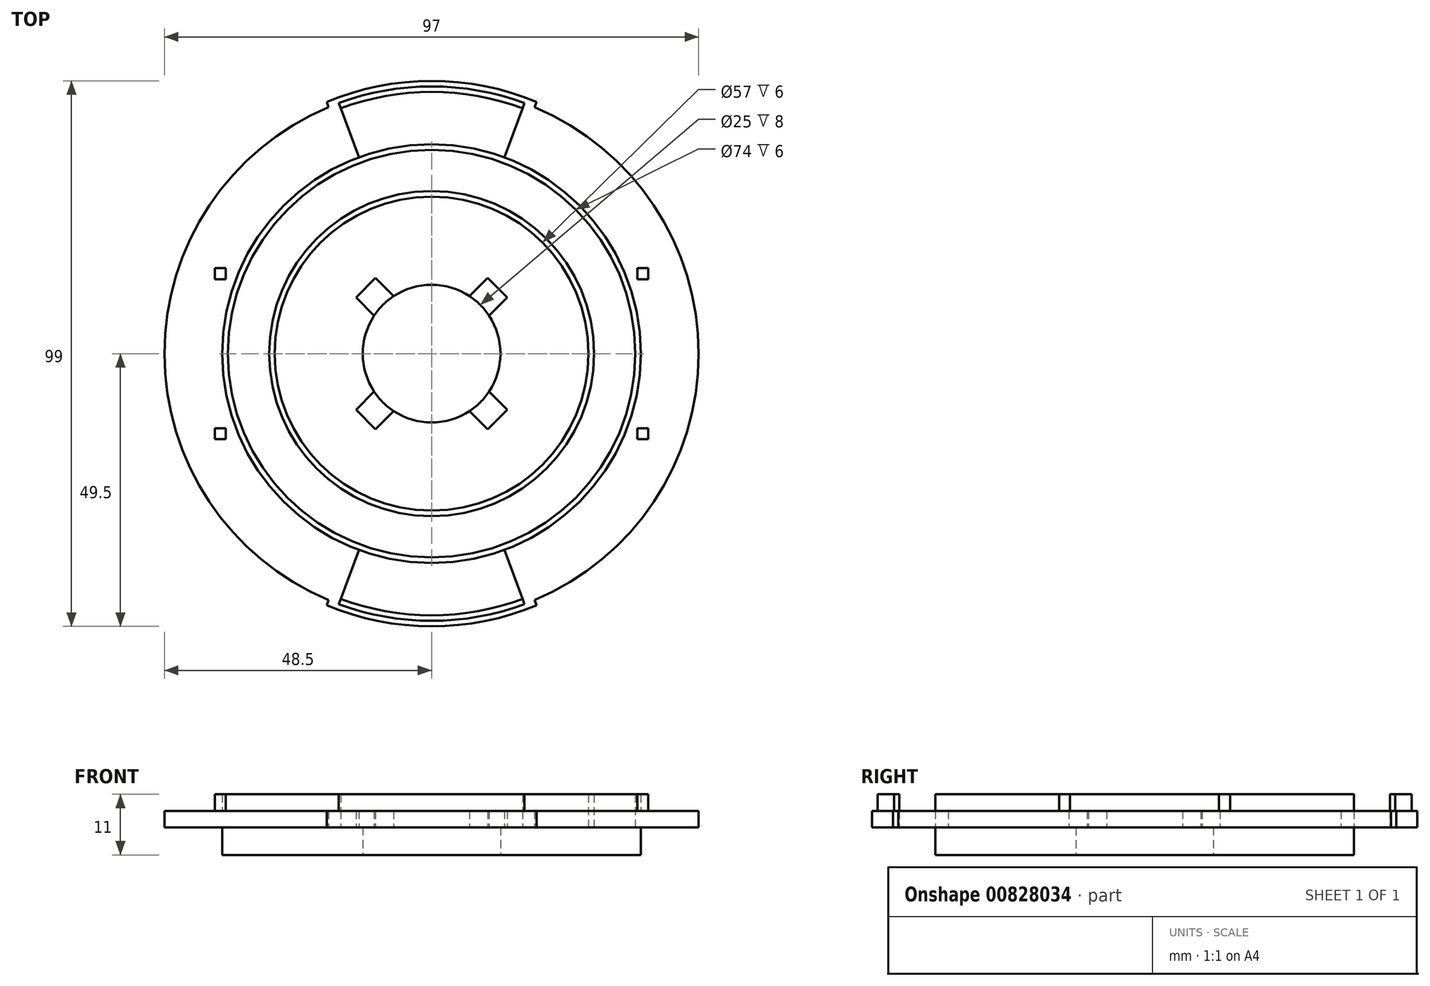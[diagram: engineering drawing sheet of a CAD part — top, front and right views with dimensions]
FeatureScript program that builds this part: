
annotation { "Feature Type Name" : "Feature", "Feature Type Description" : "" }
export const myFeature = defineFeature(function(context is Context, id is Id, definition is map)
    precondition{}
    {
        {
            var Q0;
            Q0=qCreatedBy(makeId("Top.planeOp"),FACE);
            var sketch = newSketch(context, id + "F0", { "sketchPlane" : qUnion([Q0])});
            skCircle(sketch, "E0", {"center": v(0, 0) * mm, "radius": 28.5 * mm});
            skCircle(sketch, "E1", {"center": v(0, 0) * mm, "radius": 12.5 * mm});
            skCircle(sketch, "E2", {"center": v(0, 0) * mm, "radius": 37 * mm});
            skCircle(sketch, "E3", {"center": v(0, 0) * mm, "radius": 47.5 * mm});
            skCircle(sketch, "E4", {"center": v(0, 0) * mm, "radius": 49.5 * mm});
            skCircle(sketch, "E5", {"center": v(0, 0) * mm, "radius": 38 * mm});
            skLineSegment(sketch, "E6", {"start": v(0, 0) * mm, "end": v(0, 0) * mm});
            skCircle(sketch, "E7.0", {"center": v(0, 0) * mm, "radius": 48.5 * mm});
            skLineSegment(sketch, "E8", {"start": v(0, 0) * mm, "end": v(0, 19.62) * mm, "construction": true});
            skLineSegment(sketch, "E9", {"start": v(0, 0) * mm, "end": v(17.17, 0) * mm, "construction": true});
            skPoint(sketch, "E10", {"position": v(-16.5, 44.54) * mm});
            skPoint(sketch, "E11", {"position": v(16.5, 44.54) * mm});
            skLineSegment(sketch, "E12", {"start": v(-16.85, 45.48) * mm, "end": v(-13.2, 35.63) * mm});
            skLineSegment(sketch, "E13", {"start": v(16.85, 45.48) * mm, "end": v(13.2, 35.63) * mm});
            skLineSegment(sketch, "E14.MirrorCS", {"start": v(-16.85, -45.48) * mm, "end": v(-13.2, -35.63) * mm});
            skLineSegment(sketch, "E15.MirrorCS", {"start": v(16.85, -45.48) * mm, "end": v(13.2, -35.63) * mm});
            skLineSegment(sketch, "E16", {"start": v(-18.36, 43.8) * mm, "end": v(-19.06, 45.68) * mm});
            skLineSegment(sketch, "E17.MirrorCS", {"start": v(18.36, 43.8) * mm, "end": v(19.06, 45.68) * mm});
            skLineSegment(sketch, "E18.MirrorCS", {"start": v(-18.36, -43.8) * mm, "end": v(-19.06, -45.68) * mm});
            skLineSegment(sketch, "E19.MirrorCS", {"start": v(18.36, -43.8) * mm, "end": v(19.06, -45.68) * mm});
            skCircle(sketch, "E20.0", {"center": v(0, 0) * mm, "radius": 29.5 * mm});
            skPoint(sketch, "E21.orphan", {"position": v(16.5, -44.54) * mm});
            skPoint(sketch, "E22.orphan", {"position": v(-16.5, -44.54) * mm});
            skLineSegment(sketch, "E23", {"start": v(0, 0) * mm, "end": v(14.52, 14.52) * mm, "construction": true});
            skLineSegment(sketch, "E24", {"start": v(11.95, 11.95) * mm, "end": v(10.19, 13.72) * mm});
            skLineSegment(sketch, "E25", {"start": v(10.19, 13.72) * mm, "end": v(4.7, 8.23) * mm});
            skLineSegment(sketch, "E26.MirrorCS", {"start": v(11.95, 11.95) * mm, "end": v(13.72, 10.19) * mm});
            skLineSegment(sketch, "E27.MirrorCS", {"start": v(13.72, 10.19) * mm, "end": v(8.23, 4.7) * mm});
            skLineSegment(sketch, "E28.1.0", {"start": v(-13.72, 10.19) * mm, "end": v(-8.23, 4.7) * mm});
            skLineSegment(sketch, "E28.1.1", {"start": v(-11.95, 11.95) * mm, "end": v(-10.19, 13.72) * mm});
            skLineSegment(sketch, "E28.1.2", {"start": v(-11.95, 11.95) * mm, "end": v(-13.72, 10.19) * mm});
            skLineSegment(sketch, "E28.1.3", {"start": v(-10.19, 13.72) * mm, "end": v(-4.7, 8.23) * mm});
            skLineSegment(sketch, "E28.2.0", {"start": v(-10.19, -13.72) * mm, "end": v(-4.7, -8.23) * mm});
            skLineSegment(sketch, "E28.2.1", {"start": v(-11.95, -11.95) * mm, "end": v(-13.72, -10.19) * mm});
            skLineSegment(sketch, "E28.2.2", {"start": v(-11.95, -11.95) * mm, "end": v(-10.19, -13.72) * mm});
            skLineSegment(sketch, "E28.2.3", {"start": v(-13.72, -10.19) * mm, "end": v(-8.23, -4.7) * mm});
            skLineSegment(sketch, "E28.3.0", {"start": v(13.72, -10.19) * mm, "end": v(8.23, -4.7) * mm});
            skLineSegment(sketch, "E28.3.1", {"start": v(11.95, -11.95) * mm, "end": v(10.19, -13.72) * mm});
            skLineSegment(sketch, "E28.3.2", {"start": v(11.95, -11.95) * mm, "end": v(13.72, -10.19) * mm});
            skLineSegment(sketch, "E28.3.3", {"start": v(10.19, -13.72) * mm, "end": v(4.7, -8.23) * mm});
            skLineSegment(sketch, "E29.bottom", {"start": v(39.36, 15.52) * mm, "end": v(37.36, 15.52) * mm});
            skLineSegment(sketch, "E29.top", {"start": v(39.36, 13.52) * mm, "end": v(37.36, 13.52) * mm});
            skLineSegment(sketch, "E29.left", {"start": v(39.36, 15.52) * mm, "end": v(39.36, 13.52) * mm});
            skLineSegment(sketch, "E29.right", {"start": v(37.36, 15.52) * mm, "end": v(37.36, 13.52) * mm});
            skPoint(sketch, "E29.middle", {"position": v(38.36, 14.52) * mm});
            skLineSegment(sketch, "E30.MirrorCS", {"start": v(39.36, -15.52) * mm, "end": v(37.36, -15.52) * mm});
            skLineSegment(sketch, "E31.MirrorCS", {"start": v(39.36, -15.52) * mm, "end": v(39.36, -13.52) * mm});
            skLineSegment(sketch, "E32.MirrorCS", {"start": v(39.36, -13.52) * mm, "end": v(37.36, -13.52) * mm});
            skLineSegment(sketch, "E33.MirrorCS", {"start": v(37.36, -15.52) * mm, "end": v(37.36, -13.52) * mm});
            skLineSegment(sketch, "E34.MirrorCS", {"start": v(-37.36, 15.52) * mm, "end": v(-37.36, 13.52) * mm});
            skLineSegment(sketch, "E35.MirrorCS", {"start": v(-39.36, 15.52) * mm, "end": v(-37.36, 15.52) * mm});
            skLineSegment(sketch, "E36.MirrorCS", {"start": v(-39.36, 15.52) * mm, "end": v(-39.36, 13.52) * mm});
            skLineSegment(sketch, "E37.MirrorCS", {"start": v(-39.36, 13.52) * mm, "end": v(-37.36, 13.52) * mm});
            skLineSegment(sketch, "E38.MirrorCS", {"start": v(-39.36, -13.52) * mm, "end": v(-37.36, -13.52) * mm});
            skLineSegment(sketch, "E39.MirrorCS", {"start": v(-37.36, -15.52) * mm, "end": v(-37.36, -13.52) * mm});
            skLineSegment(sketch, "E40.MirrorCS", {"start": v(-39.36, -15.52) * mm, "end": v(-37.36, -15.52) * mm});
            skLineSegment(sketch, "E41.MirrorCS", {"start": v(-39.36, -15.52) * mm, "end": v(-39.36, -13.52) * mm});
            skSolve(sketch);
        }
        {
            var Q0;
            {var subQ0=sQuery(id+"F0.wireOp",EDGE,"fbeafffa-17f5-44ee-a948-eee91f81d2460.MirrorCS");Q0=makeQuery(id+"F0.imprint","IMPRINT",FACE,{"disambiguationData":[TD([[makeQuery(id+"F0.imprint","IMPRINT",EDGE,{"derivedFrom":subQ0}),1.0]])]});}
            var Q1;
            {var subQ5=sQuery(id+"F0.wireOp",EDGE,"E3");var subQ8=makeQuery(id+"F0.imprint","INTERSECT",VERTEX,{"derivedFrom":[subQ5,sQuery(id+"F0.wireOp",EDGE,"0e935231-a2d4-4fac-a670-a3e43223463f0.MirrorCS")]});Q1=makeQuery(id+"F0.imprint","IMPRINT",FACE,{"disambiguationData":[TD([[makeQuery(id+"F0.imprint","IMPRINT",EDGE,{"disambiguationData":[TD([[subQ8,1.0]])],"derivedFrom":subQ5}),-1.0]])]});}
            var Q2;
            {var subQ0=sQuery(id+"F0.wireOp",EDGE,"7BwAZsgM-bEdh-uHs1-3V4v-wMSkKcm2EpHe");var subQ1=sQuery(id+"F0.wireOp",EDGE,"E2");var subQ2=makeQuery(id+"F0.imprint","INTERSECT",VERTEX,{"derivedFrom":[subQ1,subQ0]});Q2=makeQuery(id+"F0.imprint","IMPRINT",FACE,{"disambiguationData":[TD([[makeQuery(id+"F0.imprint","IMPRINT",EDGE,{"disambiguationData":[TD([[subQ2,1.0]])],"derivedFrom":subQ1}),-1.0]])]});}
            var Q3;
            {var subQ4=sQuery(id+"F0.wireOp",EDGE,"7BwAZsgM-bEdh-uHs1-3V4v-wMSkKcm2EpHe");var subQ6=sQuery(id+"F0.wireOp",EDGE,"E2");var subQ7=makeQuery(id+"F0.imprint","INTERSECT",VERTEX,{"derivedFrom":[subQ6,subQ4]});Q3=makeQuery(id+"F0.imprint","IMPRINT",FACE,{"disambiguationData":[TD([[makeQuery(id+"F0.imprint","IMPRINT",EDGE,{"disambiguationData":[TD([[subQ7,-1.0]])],"derivedFrom":subQ6}),-1.0]])]});}
            var Q4;
            Q4=makeQuery(id+"F0.imprint","IMPRINT",FACE,{"disambiguationData":[TD([[makeQuery(id+"F0.imprint","IMPRINT",EDGE,{"derivedFrom":sQuery(id+"F0.wireOp",EDGE,"E0")}),-1.0]])]});
            var Q5;
            {var subQ3=sQuery(id+"F0.wireOp",EDGE,"7BwAZsgM-bEdh-uHs1-3V4v-wMSkKcm2EpHe");var subQ5=sQuery(id+"F0.wireOp",EDGE,"E3");var subQ6=makeQuery(id+"F0.imprint","INTERSECT",VERTEX,{"derivedFrom":[subQ5,subQ3]});Q5=makeQuery(id+"F0.imprint","IMPRINT",FACE,{"disambiguationData":[TD([[makeQuery(id+"F0.imprint","IMPRINT",EDGE,{"disambiguationData":[TD([[subQ6,-1.0]])],"derivedFrom":subQ5}),1.0]])]});}
            var Q6;
            {var subQ1=sQuery(id+"F0.wireOp",EDGE,"E3");var subQ4=sQuery(id+"F0.wireOp",EDGE,"ac8cf38f-5c8b-4d6e-a034-1b16bb4f7d430.MirrorCS");var subQ9=makeQuery(id+"F0.imprint","INTERSECT",VERTEX,{"derivedFrom":[subQ1,subQ4]});Q6=makeQuery(id+"F0.imprint","IMPRINT",FACE,{"disambiguationData":[TD([[makeQuery(id+"F0.imprint","IMPRINT",EDGE,{"disambiguationData":[TD([[subQ9,-1.0]])],"derivedFrom":subQ1}),-1.0]])]});}
            var Q7;
            {var subQ0=sQuery(id+"F0.wireOp",EDGE,"0e935231-a2d4-4fac-a670-a3e43223463f0.MirrorCS");var subQ1=sQuery(id+"F0.wireOp",EDGE,"E2");var subQ2=makeQuery(id+"F0.imprint","INTERSECT",VERTEX,{"derivedFrom":[subQ1,subQ0]});Q7=makeQuery(id+"F0.imprint","IMPRINT",FACE,{"disambiguationData":[TD([[makeQuery(id+"F0.imprint","IMPRINT",EDGE,{"disambiguationData":[TD([[subQ2,1.0]])],"derivedFrom":subQ1}),-1.0]])]});}
            var Q8;
            {var subQ0=sQuery(id+"F0.wireOp",EDGE,"7b968056-7693-4d8b-909f-8d37a40829c0.0");var subQ1=sQuery(id+"F0.wireOp",EDGE,"E2");var subQ2=makeQuery(id+"F0.imprint","INTERSECT",VERTEX,{"derivedFrom":[subQ1,subQ0]});Q8=makeQuery(id+"F0.imprint","IMPRINT",FACE,{"disambiguationData":[TD([[makeQuery(id+"F0.imprint","IMPRINT",EDGE,{"disambiguationData":[TD([[subQ2,-1.0]])],"derivedFrom":subQ1}),-1.0]])]});}
            var Q9;
            {var subQ0=sQuery(id+"F0.wireOp",EDGE,"E18.MirrorCS");var subQ1=sQuery(id+"F0.wireOp",EDGE,"E4");var subQ2=makeQuery(id+"F0.imprint","INTERSECT",VERTEX,{"derivedFrom":[subQ1,subQ0]});Q9=makeQuery(id+"F0.imprint","IMPRINT",FACE,{"disambiguationData":[TD([[makeQuery(id+"F0.imprint","IMPRINT",EDGE,{"disambiguationData":[TD([[subQ2,-1.0]])],"derivedFrom":subQ1}),1.0]])]});}
            var Q10;
            {var subQ0=sQuery(id+"F0.wireOp",EDGE,"E16");var subQ1=sQuery(id+"F0.wireOp",EDGE,"E4");var subQ2=makeQuery(id+"F0.imprint","INTERSECT",VERTEX,{"derivedFrom":[subQ1,subQ0]});Q10=makeQuery(id+"F0.imprint","IMPRINT",FACE,{"disambiguationData":[TD([[makeQuery(id+"F0.imprint","IMPRINT",EDGE,{"disambiguationData":[TD([[subQ2,1.0]])],"derivedFrom":subQ1}),1.0]])]});}
            var Q11;
            {var subQ1=sQuery(id+"F0.wireOp",EDGE,"E28.1.1");Q11=makeQuery(id+"F0.imprint","IMPRINT",FACE,{"disambiguationData":[TD([[makeQuery(id+"F0.imprint","IMPRINT",EDGE,{"derivedFrom":subQ1}),-1.0]])]});}
            var Q12;
            {var subQ1=sQuery(id+"F0.wireOp",EDGE,"E28.3.1");Q12=makeQuery(id+"F0.imprint","IMPRINT",FACE,{"disambiguationData":[TD([[makeQuery(id+"F0.imprint","IMPRINT",EDGE,{"derivedFrom":subQ1}),-1.0]])]});}
            var Q13;
            {var subQ4=sQuery(id+"F0.wireOp",EDGE,"E28.2.1");Q13=makeQuery(id+"F0.imprint","IMPRINT",FACE,{"disambiguationData":[TD([[makeQuery(id+"F0.imprint","IMPRINT",EDGE,{"derivedFrom":subQ4}),-1.0]])]});}
            var Q14;
            {var subQ2=sQuery(id+"F0.wireOp",EDGE,"E24");Q14=makeQuery(id+"F0.imprint","IMPRINT",FACE,{"disambiguationData":[TD([[makeQuery(id+"F0.imprint","IMPRINT",EDGE,{"derivedFrom":subQ2}),1.0]])]});}
            extrude(context, id + "F1", {"entities" : qUnion([Q0, Q1, Q2, Q3, Q4, Q5, Q6, Q7, Q8, Q9, Q10, Q11, Q12, Q13, Q14]), "depth" : 3 * mm, "offsetDistance" : 25 * mm});
        }
        {
            var Q0;
            Q0=makeQuery(id+"F0.imprint","IMPRINT",FACE,{"disambiguationData":[TD([[makeQuery(id+"F0.imprint","IMPRINT",EDGE,{"derivedFrom":sQuery(id+"F0.wireOp",EDGE,"E0")}),1.0]])]});
            var Q1;
            Q1=makeQuery(id+"F0.imprint","IMPRINT",FACE,{"disambiguationData":[TD([[makeQuery(id+"F0.imprint","IMPRINT",EDGE,{"derivedFrom":sQuery(id+"F0.wireOp",EDGE,"E0")}),-1.0]])]});
            var Q2;
            {var subQ5=sQuery(id+"F0.wireOp",EDGE,"7BwAZsgM-bEdh-uHs1-3V4v-wMSkKcm2EpHe");var subQ7=sQuery(id+"F0.wireOp",EDGE,"E2");var subQ9=makeQuery(id+"F0.imprint","INTERSECT",VERTEX,{"derivedFrom":[subQ7,subQ5]});Q2=makeQuery(id+"F0.imprint","IMPRINT",FACE,{"disambiguationData":[TD([[makeQuery(id+"F0.imprint","IMPRINT",EDGE,{"disambiguationData":[TD([[subQ9,-1.0]])],"derivedFrom":subQ7}),-1.0]])]});}
            var Q3;
            Q3=makeQuery(id+"F0.imprint","IMPRINT",FACE,{"disambiguationData":[TD([[makeQuery(id+"F0.imprint","IMPRINT",EDGE,{"derivedFrom":sQuery(id+"F0.wireOp",EDGE,"E2")}),1.0]])]});
            var Q4;
            {var subQ1=sQuery(id+"F0.wireOp",EDGE,"E28.1.1");Q4=makeQuery(id+"F0.imprint","IMPRINT",FACE,{"disambiguationData":[TD([[makeQuery(id+"F0.imprint","IMPRINT",EDGE,{"derivedFrom":subQ1}),-1.0]])]});}
            var Q5;
            {var subQ2=sQuery(id+"F0.wireOp",EDGE,"E24");Q5=makeQuery(id+"F0.imprint","IMPRINT",FACE,{"disambiguationData":[TD([[makeQuery(id+"F0.imprint","IMPRINT",EDGE,{"derivedFrom":subQ2}),1.0]])]});}
            var Q6;
            {var subQ1=sQuery(id+"F0.wireOp",EDGE,"E28.3.1");Q6=makeQuery(id+"F0.imprint","IMPRINT",FACE,{"disambiguationData":[TD([[makeQuery(id+"F0.imprint","IMPRINT",EDGE,{"derivedFrom":subQ1}),-1.0]])]});}
            var Q7;
            {var subQ4=sQuery(id+"F0.wireOp",EDGE,"E28.2.1");Q7=makeQuery(id+"F0.imprint","IMPRINT",FACE,{"disambiguationData":[TD([[makeQuery(id+"F0.imprint","IMPRINT",EDGE,{"derivedFrom":subQ4}),-1.0]])]});}
            extrude(context, id + "F2", {"entities" : qUnion([Q0, Q1, Q2, Q3, Q4, Q5, Q6, Q7]), "operationType" : NewBodyOperationType.ADD, "oppositeDirection" : true, "depth" : 5 * mm, "offsetDistance" : 25 * mm});
        }
        {
            var Q0;
            {var subQ0=sQuery(id+"F0.wireOp",EDGE,"E13");var subQ1=sQuery(id+"F0.wireOp",EDGE,"E3");var subQ2=makeQuery(id+"F0.imprint","INTERSECT",VERTEX,{"derivedFrom":[subQ1,subQ0]});Q0=makeQuery(id+"F0.imprint","IMPRINT",FACE,{"disambiguationData":[TD([[makeQuery(id+"F0.imprint","IMPRINT",EDGE,{"disambiguationData":[TD([[subQ2,-1.0]])],"derivedFrom":subQ1}),-1.0]])]});}
            var Q1;
            {var subQ0=sQuery(id+"F0.wireOp",EDGE,"E14.MirrorCS");var subQ1=sQuery(id+"F0.wireOp",EDGE,"E3");var subQ2=makeQuery(id+"F0.imprint","INTERSECT",VERTEX,{"derivedFrom":[subQ1,subQ0]});Q1=makeQuery(id+"F0.imprint","IMPRINT",FACE,{"disambiguationData":[TD([[makeQuery(id+"F0.imprint","IMPRINT",EDGE,{"disambiguationData":[TD([[subQ2,-1.0]])],"derivedFrom":subQ1}),-1.0]])]});}
            var Q2;
            Q2=makeQuery(id+"F0.imprint","IMPRINT",FACE,{"disambiguationData":[TD([[makeQuery(id+"F0.imprint","IMPRINT",EDGE,{"derivedFrom":sQuery(id+"F0.wireOp",EDGE,"E2")}),-1.0]])]});
            var Q3;
            Q3=makeQuery(id+"F0.imprint","IMPRINT",FACE,{"disambiguationData":[TD([[makeQuery(id+"F0.imprint","IMPRINT",EDGE,{"derivedFrom":sQuery(id+"F0.wireOp",EDGE,"E0")}),-1.0]])]});
            var Q4;
            Q4=makeQuery(id+"F0.imprint","IMPRINT",FACE,{"disambiguationData":[TD([[makeQuery(id+"F0.imprint","IMPRINT",EDGE,{"derivedFrom":sQuery(id+"F0.wireOp",EDGE,"E38.MirrorCS")}),-1.0]])]});
            var Q5;
            Q5=makeQuery(id+"F0.imprint","IMPRINT",FACE,{"disambiguationData":[TD([[makeQuery(id+"F0.imprint","IMPRINT",EDGE,{"derivedFrom":sQuery(id+"F0.wireOp",EDGE,"E34.MirrorCS")}),-1.0]])]});
            var Q6;
            Q6=makeQuery(id+"F0.imprint","IMPRINT",FACE,{"disambiguationData":[TD([[makeQuery(id+"F0.imprint","IMPRINT",EDGE,{"derivedFrom":sQuery(id+"F0.wireOp",EDGE,"E30.MirrorCS")}),-1.0]])]});
            var Q7;
            Q7=makeQuery(id+"F0.imprint","IMPRINT",FACE,{"disambiguationData":[TD([[makeQuery(id+"F0.imprint","IMPRINT",EDGE,{"derivedFrom":sQuery(id+"F0.wireOp",EDGE,"E29.bottom")}),1.0]])]});
            extrude(context, id + "F3", {"entities" : qUnion([Q0, Q1, Q2, Q3, Q4, Q5, Q6, Q7]), "operationType" : NewBodyOperationType.ADD, "depth" : 6 * mm, "offsetDistance" : 25 * mm});
        }
    });
